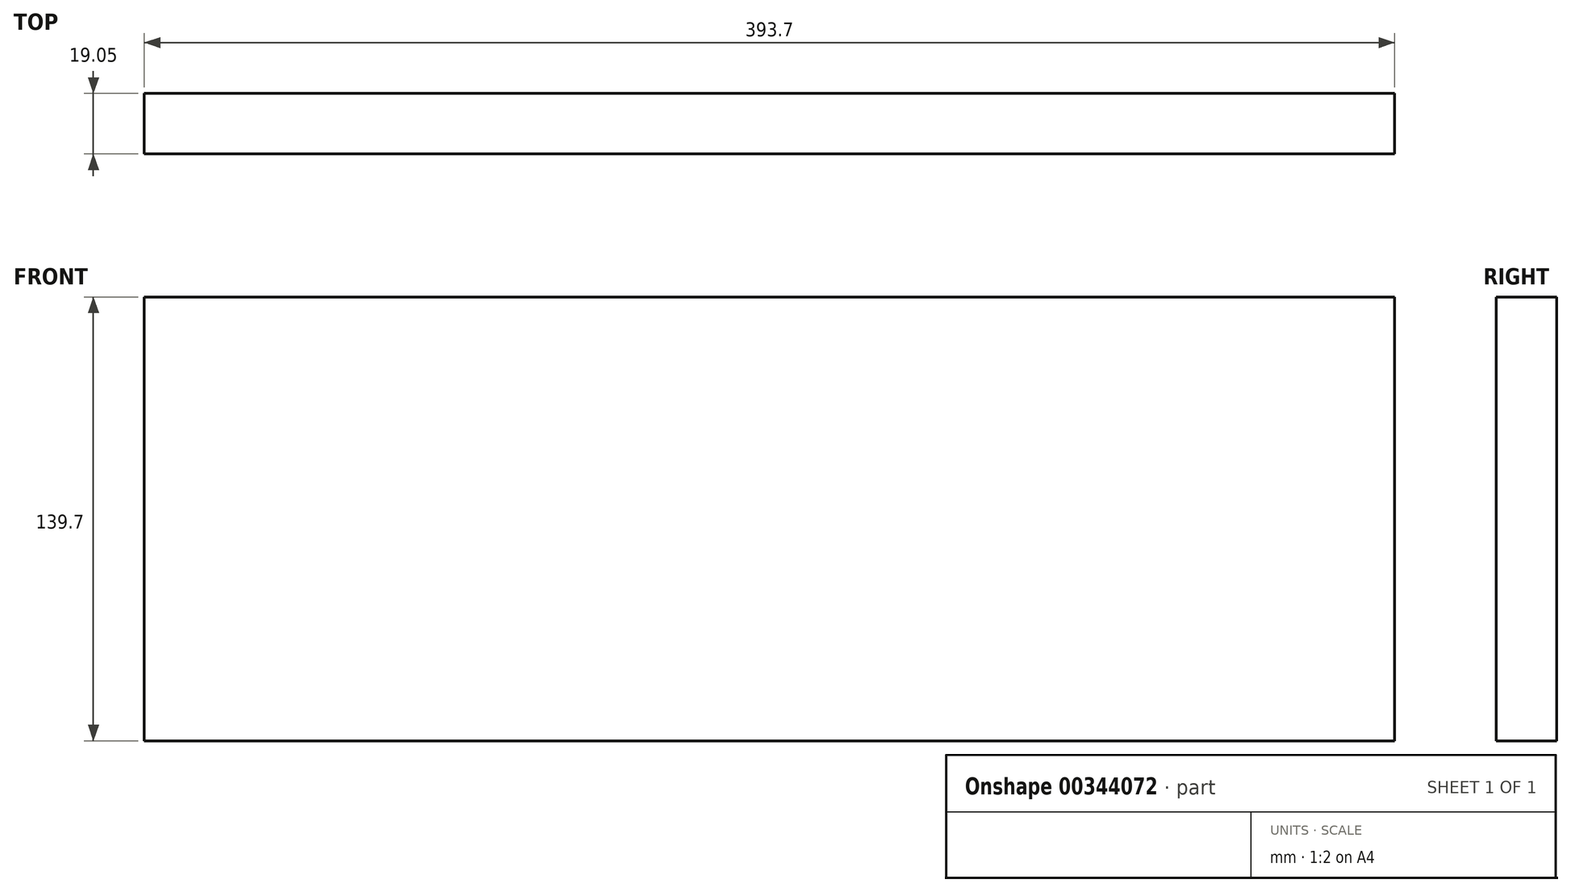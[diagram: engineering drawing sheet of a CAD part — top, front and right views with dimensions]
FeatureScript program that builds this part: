
annotation { "Feature Type Name" : "Feature", "Feature Type Description" : "" }
export const myFeature = defineFeature(function(context is Context, id is Id, definition is map)
    precondition{}
    {
        {
            var Q0;
            Q0=qCreatedBy(makeId("Front.planeOp"),FACE);
            var sketch = newSketch(context, id + "F0", { "sketchPlane" : qUnion([Q0])});
            skLineSegment(sketch, "E0.bottom", {"start": v(0, 0) * mm, "end": v(393.7, 0) * mm});
            skLineSegment(sketch, "E0.top", {"start": v(0, 139.7) * mm, "end": v(393.7, 139.7) * mm});
            skLineSegment(sketch, "E0.left", {"start": v(0, 0) * mm, "end": v(0, 139.7) * mm});
            skLineSegment(sketch, "E0.right", {"start": v(393.7, 0) * mm, "end": v(393.7, 139.7) * mm});
            skSolve(sketch);
        }
        {
            var Q0;
            Q0=qSketchRegion(id+"F0",true);
            extrude(context, id + "F1", {"entities" : qUnion([Q0]), "depth" : 19.05 * mm});
        }
    });
